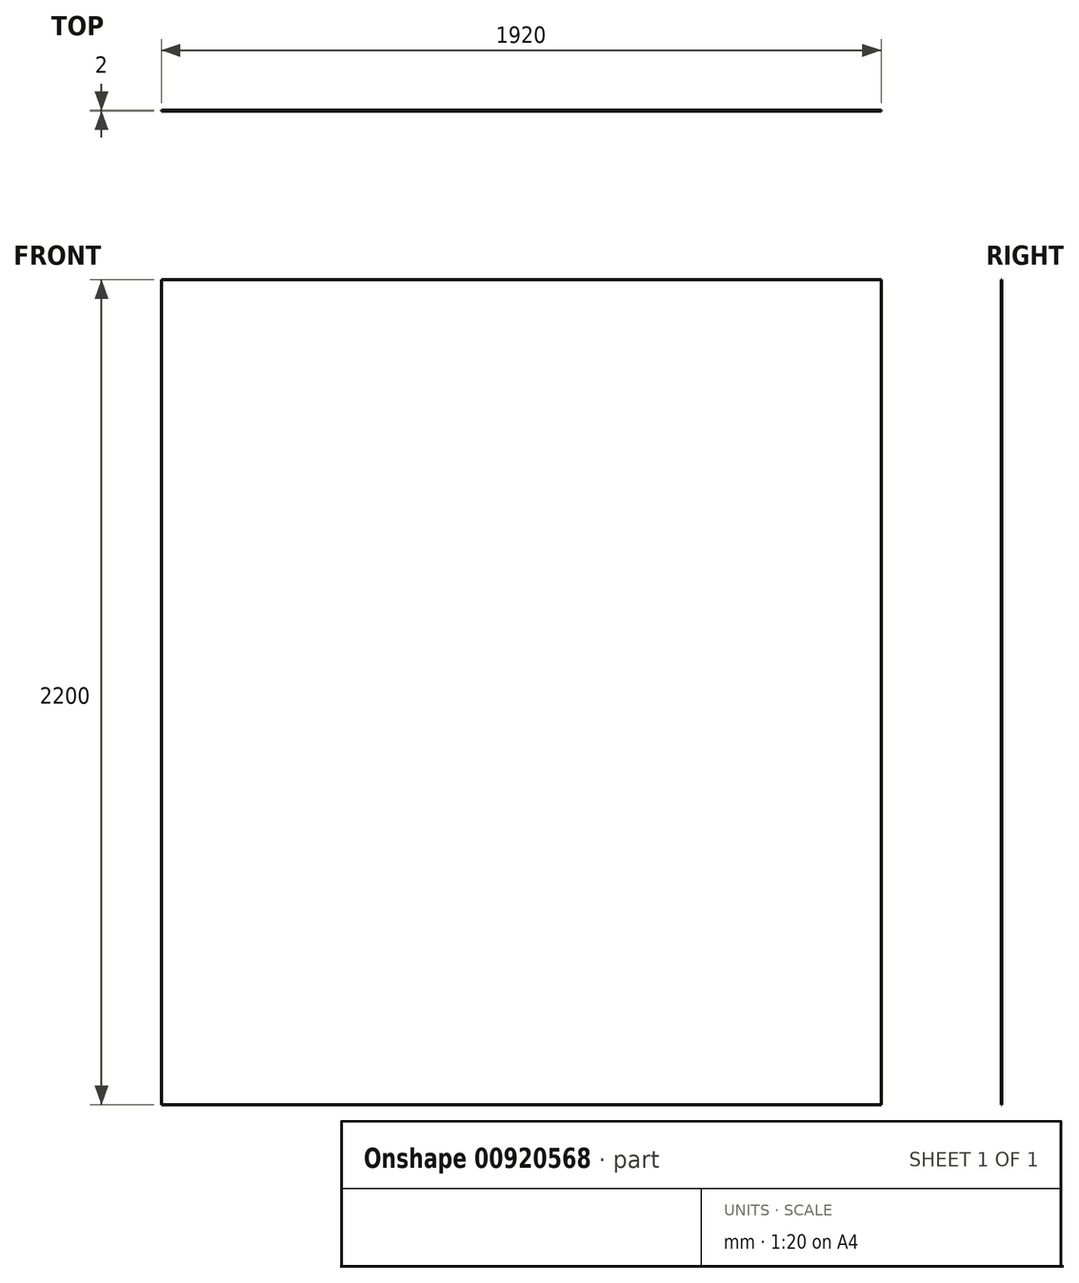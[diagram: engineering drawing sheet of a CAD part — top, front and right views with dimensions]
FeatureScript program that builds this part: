
annotation { "Feature Type Name" : "Feature", "Feature Type Description" : "" }
export const myFeature = defineFeature(function(context is Context, id is Id, definition is map)
    precondition{}
    {
        {
            var Q0;
            Q0=qCreatedBy(makeId("Front.planeOp"),FACE);
            var sketch = newSketch(context, id + "F0", { "sketchPlane" : qUnion([Q0])});
            skLineSegment(sketch, "E0.bottom", {"start": v(960, -1100) * mm, "end": v(-960, -1100) * mm});
            skLineSegment(sketch, "E0.top", {"start": v(960, 1100) * mm, "end": v(-960, 1100) * mm});
            skLineSegment(sketch, "E0.left", {"start": v(960, -1100) * mm, "end": v(960, 1100) * mm});
            skLineSegment(sketch, "E0.right", {"start": v(-960, -1100) * mm, "end": v(-960, 1100) * mm});
            skPoint(sketch, "E0.middle", {"position": v(0, 0) * mm});
            skSolve(sketch);
        }
        {
            var Q0;
            Q0 = qSketchRegion(id + "F0", true);
            extrude(context, id + "F1", {"entities" : qUnion([Q0]), "depth" : 2 * mm, "offsetDistance" : 25 * mm, "symmetric" : true});
        }
    });
